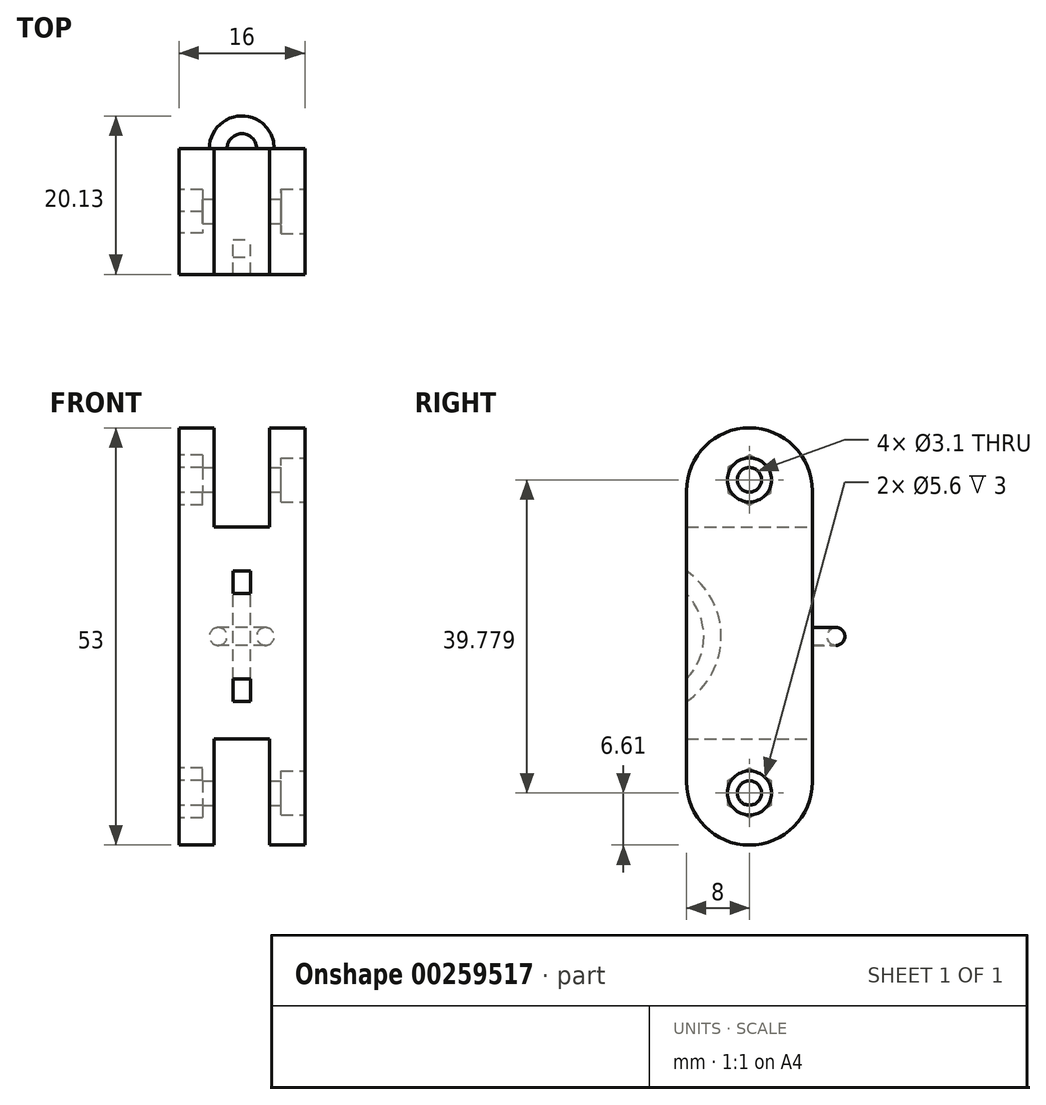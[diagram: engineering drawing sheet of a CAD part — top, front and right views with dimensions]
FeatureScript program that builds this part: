
annotation { "Feature Type Name" : "Feature", "Feature Type Description" : "" }
export const myFeature = defineFeature(function(context is Context, id is Id, definition is map)
    precondition{}
    {
        {
            var Q0;
            Q0=qCreatedBy(makeId("Front.planeOp"),FACE);
            var sketch = newSketch(context, id + "F0", { "sketchPlane" : qUnion([Q0])});
            skLineSegment(sketch, "E0", {"start": v(8, 18) * mm, "end": v(8, -18) * mm});
            skLineSegment(sketch, "E1", {"start": v(-8, -18) * mm, "end": v(-8, 18) * mm});
            skLineSegment(sketch, "E2", {"start": v(-8, 18) * mm, "end": v(-8, 26.5) * mm});
            skLineSegment(sketch, "E3", {"start": v(-8, 26.5) * mm, "end": v(-3.5, 26.5) * mm});
            skLineSegment(sketch, "E4.MirrorCS", {"start": v(8, 26.5) * mm, "end": v(3.5, 26.5) * mm});
            skLineSegment(sketch, "E5.MirrorCS", {"start": v(8, 18) * mm, "end": v(8, 26.5) * mm});
            skLineSegment(sketch, "E6.MirrorCS", {"start": v(-3.5, -26.5) * mm, "end": v(-3.5, -18) * mm});
            skLineSegment(sketch, "E7.MirrorCS", {"start": v(8, -18) * mm, "end": v(8, -26.5) * mm});
            skLineSegment(sketch, "E8.MirrorCS", {"start": v(-8, -18) * mm, "end": v(-8, -26.5) * mm});
            skLineSegment(sketch, "E9.MirrorCS", {"start": v(3.5, -26.5) * mm, "end": v(3.5, -18) * mm});
            skLineSegment(sketch, "E10.MirrorCS", {"start": v(-8, -26.5) * mm, "end": v(-3.5, -26.5) * mm});
            skLineSegment(sketch, "E11.MirrorCS", {"start": v(8, -26.5) * mm, "end": v(3.5, -26.5) * mm});
            skLineSegment(sketch, "E12", {"start": v(3.5, 13.9) * mm, "end": v(-3.5, 13.9) * mm});
            skLineSegment(sketch, "E13", {"start": v(3.5, 26.5) * mm, "end": v(3.5, 13.9) * mm});
            skLineSegment(sketch, "E14", {"start": v(-3.5, 26.5) * mm, "end": v(-3.5, 13.9) * mm});
            skLineSegment(sketch, "E15", {"start": v(3.5, -18) * mm, "end": v(3.5, -13) * mm});
            skLineSegment(sketch, "E16", {"start": v(3.5, -13) * mm, "end": v(-3.5, -13) * mm});
            skLineSegment(sketch, "E17", {"start": v(-3.5, -13) * mm, "end": v(-3.5, -18) * mm});
            skSolve(sketch);
        }
        {
            var Q0;
            Q0 = qSketchRegion(id + "F0", true);
            extrude(context, id + "F1", {"entities" : qUnion([Q0]), "depth" : 16 * mm});
        }
        {
            var Q0;
            Q0=makeQuery(id+"F1.opExtrude","CAP_EDGE",EDGE,{"disambiguationData":[OSD([sQuery(id+"F0.wireOp",EDGE,"E4.MirrorCS")])],"isStart":false});
            var Q1;
            Q1=makeQuery(id+"F1.opExtrude","CAP_EDGE",EDGE,{"disambiguationData":[OSD([sQuery(id+"F0.wireOp",EDGE,"E3")])],"isStart":false});
            var Q2;
            Q2=makeQuery(id+"F1.opExtrude","CAP_EDGE",EDGE,{"disambiguationData":[OSD([sQuery(id+"F0.wireOp",EDGE,"E3")])],"isStart":true});
            var Q3;
            Q3=makeQuery(id+"F1.opExtrude","CAP_EDGE",EDGE,{"disambiguationData":[OSD([sQuery(id+"F0.wireOp",EDGE,"E4.MirrorCS")])],"isStart":true});
            var Q4;
            Q4=makeQuery(id+"F1.opExtrude","CAP_EDGE",EDGE,{"disambiguationData":[OSD([sQuery(id+"F0.wireOp",EDGE,"E11.MirrorCS")])],"isStart":false});
            var Q5;
            Q5=makeQuery(id+"F1.opExtrude","CAP_EDGE",EDGE,{"disambiguationData":[OSD([sQuery(id+"F0.wireOp",EDGE,"E10.MirrorCS")])],"isStart":false});
            var Q6;
            Q6=makeQuery(id+"F1.opExtrude","CAP_EDGE",EDGE,{"disambiguationData":[OSD([sQuery(id+"F0.wireOp",EDGE,"E11.MirrorCS")])],"isStart":true});
            var Q7;
            Q7=makeQuery(id+"F1.opExtrude","CAP_EDGE",EDGE,{"disambiguationData":[OSD([sQuery(id+"F0.wireOp",EDGE,"E10.MirrorCS")])],"isStart":true});
            fillet(context, id + "F2", {"entities" : qUnion([Q0, Q1, Q2, Q3, Q4, Q5, Q6, Q7]), "radius" : 8 * mm, "tangentPropagation" : true, "allowEdgeOverflow" : false});
        }
        {
            var Q0;
            Q0=makeQuery(id+"F1.opExtrude","SWEPT_FACE",FACE,{"disambiguationData":[OSD([sQuery(id+"F0.wireOp",EDGE,"E0"),sQuery(id+"F0.wireOp",EDGE,"E5.MirrorCS"),sQuery(id+"F0.wireOp",EDGE,"E7.MirrorCS")])]});
            var sketch = newSketch(context, id + "F3", { "sketchPlane" : qUnion([Q0])});
            skCircle(sketch, "E18", {"center": v(-8, 19.89) * mm, "radius": 1.55 * mm});
            skCircle(sketch, "E19.MirrorC", {"center": v(-8, -19.89) * mm, "radius": 1.55 * mm});
            skSolve(sketch);
        }
        {
            var Q0;
            Q0 = qSketchRegion(id + "F3", true);
            extrude(context, id + "F4", {"entities" : qUnion([Q0]), "operationType" : NewBodyOperationType.REMOVE, "endBound" : BoundingType.SYMMETRIC, "oppositeDirection" : true, "depth" : 25 * mm});
        }
        {
            var Q0;
            Q0 = qSketchRegion(id + "F3", true);
            extrude(context, id + "F5", {"entities" : qUnion([Q0]), "operationType" : NewBodyOperationType.REMOVE, "oppositeDirection" : true, "depth" : 25 * mm});
        }
        {
            var Q0;
            Q0=makeQuery(id+"F1.opExtrude","SWEPT_FACE",FACE,{"disambiguationData":[OSD([sQuery(id+"F0.wireOp",EDGE,"E0"),sQuery(id+"F0.wireOp",EDGE,"E5.MirrorCS"),sQuery(id+"F0.wireOp",EDGE,"E7.MirrorCS")])]});
            var sketch = newSketch(context, id + "F6", { "sketchPlane" : qUnion([Q0])});
            skCircle(sketch, "E20", {"center": v(-8, 19.89) * mm, "radius": 2.8 * mm});
            skCircle(sketch, "E21.MirrorC", {"center": v(-8, -19.89) * mm, "radius": 2.8 * mm});
            skSolve(sketch);
        }
        {
            var Q0;
            Q0 = qSketchRegion(id + "F6", true);
            extrude(context, id + "F7", {"entities" : qUnion([Q0]), "operationType" : NewBodyOperationType.REMOVE, "oppositeDirection" : true, "depth" : 3 * mm});
        }
        {
            var Q0;
            Q0=makeQuery(id+"F1.opExtrude","SWEPT_FACE",FACE,{"disambiguationData":[OSD([sQuery(id+"F0.wireOp",EDGE,"E1"),sQuery(id+"F0.wireOp",EDGE,"E2"),sQuery(id+"F0.wireOp",EDGE,"E8.MirrorCS")])]});
            var sketch = newSketch(context, id + "F8", { "sketchPlane" : qUnion([Q0])});
            skLineSegment(sketch, "E22.0", {"start": v(10.75, 21.48) * mm, "end": v(10.75, 18.3) * mm});
            skLineSegment(sketch, "E22.1", {"start": v(10.75, 18.3) * mm, "end": v(8, 16.71) * mm});
            skLineSegment(sketch, "E22.2", {"start": v(8, 16.71) * mm, "end": v(5.25, 18.3) * mm});
            skLineSegment(sketch, "E22.3", {"start": v(5.25, 18.3) * mm, "end": v(5.25, 21.48) * mm});
            skLineSegment(sketch, "E22.4", {"start": v(5.25, 21.48) * mm, "end": v(8, 23.07) * mm});
            skLineSegment(sketch, "E22.5", {"start": v(8, 23.07) * mm, "end": v(10.75, 21.48) * mm});
            skLineSegment(sketch, "E23.MirrorCS", {"start": v(5.25, -21.48) * mm, "end": v(8, -23.07) * mm});
            skLineSegment(sketch, "E24.MirrorCS", {"start": v(10.75, -18.3) * mm, "end": v(8, -16.71) * mm});
            skLineSegment(sketch, "E25.MirrorCS", {"start": v(8, -16.71) * mm, "end": v(5.25, -18.3) * mm});
            skLineSegment(sketch, "E26.MirrorCS", {"start": v(8, -23.07) * mm, "end": v(10.75, -21.48) * mm});
            skLineSegment(sketch, "E27.MirrorCS", {"start": v(5.25, -18.3) * mm, "end": v(5.25, -21.48) * mm});
            skLineSegment(sketch, "E28.MirrorCS", {"start": v(10.75, -21.48) * mm, "end": v(10.75, -18.3) * mm});
            skSolve(sketch);
        }
        {
            var Q0;
            Q0 = qSketchRegion(id + "F8", true);
            extrude(context, id + "F9", {"entities" : qUnion([Q0]), "operationType" : NewBodyOperationType.REMOVE, "oppositeDirection" : true, "depth" : 3 * mm});
        }
        {
            var Q0;
            Q0=makeQuery(id+"F1.opExtrude","CAP_FACE",FACE,{"disambiguationData":[OSD([sQuery(id+"F0.wireOp",EDGE,"E0"),sQuery(id+"F0.wireOp",EDGE,"E1"),sQuery(id+"F0.wireOp",EDGE,"E2"),sQuery(id+"F0.wireOp",EDGE,"E3"),sQuery(id+"F0.wireOp",EDGE,"E4.MirrorCS"),sQuery(id+"F0.wireOp",EDGE,"E5.MirrorCS"),sQuery(id+"F0.wireOp",EDGE,"E6.MirrorCS"),sQuery(id+"F0.wireOp",EDGE,"E7.MirrorCS"),sQuery(id+"F0.wireOp",EDGE,"E8.MirrorCS"),sQuery(id+"F0.wireOp",EDGE,"E9.MirrorCS"),sQuery(id+"F0.wireOp",EDGE,"E10.MirrorCS"),sQuery(id+"F0.wireOp",EDGE,"E11.MirrorCS"),sQuery(id+"F0.wireOp",EDGE,"E12"),sQuery(id+"F0.wireOp",EDGE,"E13"),sQuery(id+"F0.wireOp",EDGE,"E14"),sQuery(id+"F0.wireOp",EDGE,"E15"),sQuery(id+"F0.wireOp",EDGE,"E16"),sQuery(id+"F0.wireOp",EDGE,"E17")])],"isStart":false});
            var sketch = newSketch(context, id + "F10", { "sketchPlane" : qUnion([Q0])});
            skLineSegment(sketch, "E29", {"start": v(0, 1.86) * mm, "end": v(0, -1.74) * mm});
            skCircle(sketch, "E30", {"center": v(-3, 0) * mm, "radius": 1.13 * mm});
            skSolve(sketch);
        }
        {
            var Q0;
            Q0=makeQuery(id+"F10.imprint","IMPRINT",FACE,{"disambiguationData":[TD([[makeQuery(id+"F10.imprint","IMPRINT",EDGE,{"derivedFrom":sQuery(id+"F10.wireOp",EDGE,"E30")}),1.0]])]});
            var Q1;
            Q1=sQuery(id+"F10.wireOp",EDGE,"E29");
            revolve(context, id + "F11", {"operationType" : NewBodyOperationType.ADD, "entities" : qUnion([Q0]), "axis" : qUnion([Q1]), "revolveType" : RevolveType.FULL});
        }
        {
            var Q0;
            Q0=makeQuery(id+"F1.opExtrude","CAP_FACE",FACE,{"disambiguationData":[OSD([sQuery(id+"F0.wireOp",EDGE,"E0"),sQuery(id+"F0.wireOp",EDGE,"E1"),sQuery(id+"F0.wireOp",EDGE,"E2"),sQuery(id+"F0.wireOp",EDGE,"E3"),sQuery(id+"F0.wireOp",EDGE,"E4.MirrorCS"),sQuery(id+"F0.wireOp",EDGE,"E5.MirrorCS"),sQuery(id+"F0.wireOp",EDGE,"E6.MirrorCS"),sQuery(id+"F0.wireOp",EDGE,"E7.MirrorCS"),sQuery(id+"F0.wireOp",EDGE,"E8.MirrorCS"),sQuery(id+"F0.wireOp",EDGE,"E9.MirrorCS"),sQuery(id+"F0.wireOp",EDGE,"E10.MirrorCS"),sQuery(id+"F0.wireOp",EDGE,"E11.MirrorCS"),sQuery(id+"F0.wireOp",EDGE,"E12"),sQuery(id+"F0.wireOp",EDGE,"E13"),sQuery(id+"F0.wireOp",EDGE,"E14"),sQuery(id+"F0.wireOp",EDGE,"E15"),sQuery(id+"F0.wireOp",EDGE,"E16"),sQuery(id+"F0.wireOp",EDGE,"E17")])],"isStart":true});
            var sketch = newSketch(context, id + "F12", { "sketchPlane" : qUnion([Q0])});
            skCircle(sketch, "E31", {"center": v(3, 0) * mm, "radius": 1.13 * mm});
            skLineSegment(sketch, "E32", {"start": v(0, 5.26) * mm, "end": v(0, -4.23) * mm});
            skSolve(sketch);
        }
        {
            var Q0;
            Q0=makeQuery(id+"F12.imprint","IMPRINT",FACE,{"disambiguationData":[TD([[makeQuery(id+"F12.imprint","IMPRINT",EDGE,{"derivedFrom":sQuery(id+"F12.wireOp",EDGE,"E31")}),1.0]])]});
            var Q1;
            Q1=sQuery(id+"F12.wireOp",EDGE,"E32");
            revolve(context, id + "F13", {"operationType" : NewBodyOperationType.ADD, "entities" : qUnion([Q0]), "axis" : qUnion([Q1]), "revolveType" : RevolveType.FULL});
        }
        {
            var Q0;
            Q0=qCreatedBy(makeId("Top.planeOp"),FACE);
            var sketch = newSketch(context, id + "F14", { "sketchPlane" : qUnion([Q0])});
            skLineSegment(sketch, "E33", {"start": v(-1.88, -16) * mm, "end": v(1.88, -16) * mm});
            skLineSegment(sketch, "E34", {"start": v(4.12, -16) * mm, "end": v(8, -16) * mm});
            skLineSegment(sketch, "E35", {"start": v(-8, -16) * mm, "end": v(-4.12, -16) * mm});
            skLineSegment(sketch, "E36.bottom", {"start": v(-8, -16) * mm, "end": v(8, -16) * mm});
            skLineSegment(sketch, "E36.top", {"start": v(-8, -21.55) * mm, "end": v(8, -21.55) * mm});
            skLineSegment(sketch, "E36.left", {"start": v(-8, -16) * mm, "end": v(-8, -21.55) * mm});
            skLineSegment(sketch, "E36.right", {"start": v(8, -16) * mm, "end": v(8, -21.55) * mm});
            skSolve(sketch);
        }
        {
            var Q0;
            Q0=makeQuery(id+"F14.imprint","IMPRINT",FACE,{"disambiguationData":[TD([[makeQuery(id+"F14.imprint","IMPRINT",EDGE,{"derivedFrom":sQuery(id+"F14.wireOp",EDGE,"E36.top")}),1.0]])]});
            extrude(context, id + "F15", {"entities" : qUnion([Q0]), "operationType" : NewBodyOperationType.REMOVE, "endBound" : BoundingType.SYMMETRIC, "oppositeDirection" : true, "depth" : 25 * mm});
        }
        {
            var Q0;
            Q0=qCreatedBy(makeId("Right.planeOp"),FACE);
            var sketch = newSketch(context, id + "F16", { "sketchPlane" : qUnion([Q0])});
            skArc(sketch, "E37", {"start": v(-16, -8.28) * mm, "mid": v(-11.6, 0) * mm, "end": v(-16, 8.28) * mm});
            skArc(sketch, "E38", {"start": v(-16, -5.43) * mm, "mid": v(-13.8, 0) * mm, "end": v(-16, 5.43) * mm});
            skLineSegment(sketch, "E39", {"start": v(-16, 8.28) * mm, "end": v(-16, 5.43) * mm});
            skPoint(sketch, "E40.orphan", {"position": v(-16, 13.9) * mm});
            skLineSegment(sketch, "E41.trimOffspring", {"start": v(-16, -5.43) * mm, "end": v(-16, -8.28) * mm});
            skPoint(sketch, "E42.orphan", {"position": v(-16, -13) * mm});
            skSolve(sketch);
        }
        {
            var Q0;
            Q0 = qSketchRegion(id + "F16", true);
            extrude(context, id + "F17", {"entities" : qUnion([Q0]), "operationType" : NewBodyOperationType.REMOVE, "endBound" : BoundingType.SYMMETRIC, "oppositeDirection" : true, "depth" : 2.2 * mm});
        }
    });
